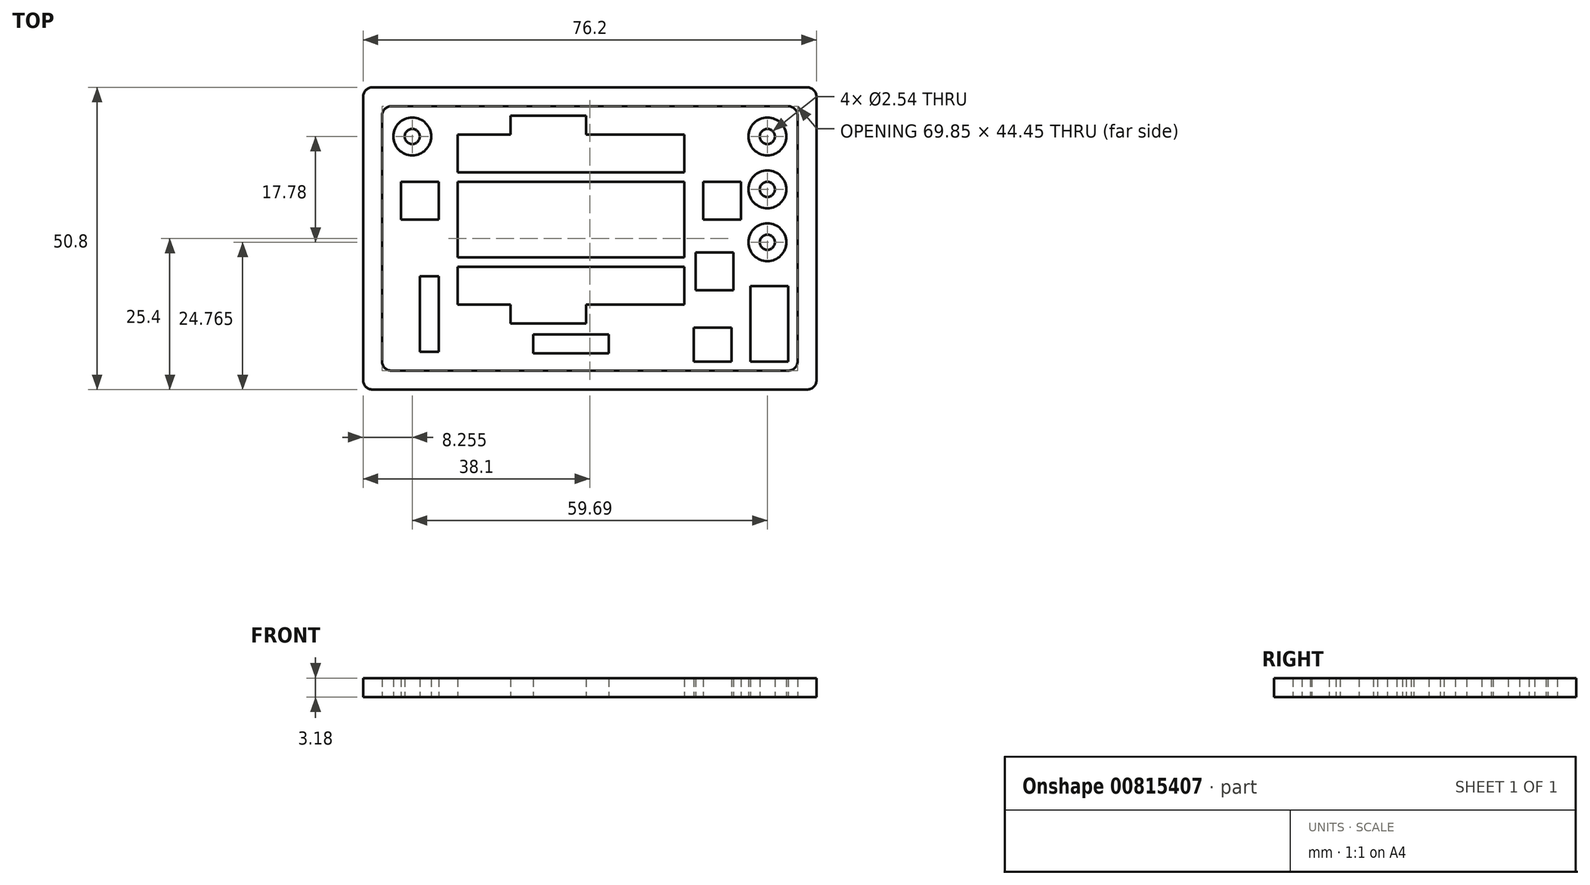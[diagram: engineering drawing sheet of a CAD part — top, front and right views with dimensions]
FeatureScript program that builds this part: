
annotation { "Feature Type Name" : "Feature", "Feature Type Description" : "" }
export const myFeature = defineFeature(function(context is Context, id is Id, definition is map)
    precondition{}
    {
        {
            var Q0;
            Q0=qCreatedBy(makeId("Top.planeOp"),FACE);
            var sketch = newSketch(context, id + "F0", { "sketchPlane" : qUnion([Q0])});
            skLineSegment(sketch, "E0.bottom", {"start": v(1.59, 0) * mm, "end": v(74.61, 0) * mm});
            skLineSegment(sketch, "E0.top", {"start": v(1.59, 50.8) * mm, "end": v(74.61, 50.8) * mm});
            skLineSegment(sketch, "E0.left", {"start": v(0, 1.59) * mm, "end": v(0, 49.21) * mm});
            skLineSegment(sketch, "E0.right", {"start": v(76.2, 1.59) * mm, "end": v(76.2, 49.21) * mm});
            skLineSegment(sketch, "E1.0", {"start": v(73.02, 4.76) * mm, "end": v(73.02, 46.04) * mm});
            skLineSegment(sketch, "E1.1", {"start": v(4.76, 3.17) * mm, "end": v(71.44, 3.17) * mm});
            skLineSegment(sketch, "E1.2", {"start": v(3.17, 4.76) * mm, "end": v(3.17, 46.04) * mm});
            skLineSegment(sketch, "E1.3", {"start": v(4.76, 47.63) * mm, "end": v(71.44, 47.63) * mm});
            skPoint(sketch, "E2.visualSharp", {"position": v(0, 50.8) * mm});
            skArc(sketch, "E2.filletArc", {"start": v(1.59, 50.8) * mm, "mid": v(0.46, 50.34) * mm, "end": v(0, 49.21) * mm});
            skPoint(sketch, "E3.visualSharp", {"position": v(76.2, 50.8) * mm});
            skArc(sketch, "E3.filletArc", {"start": v(76.2, 49.21) * mm, "mid": v(75.74, 50.34) * mm, "end": v(74.61, 50.8) * mm});
            skPoint(sketch, "E4.visualSharp", {"position": v(76.2, 0) * mm});
            skArc(sketch, "E4.filletArc", {"start": v(74.61, 0) * mm, "mid": v(75.74, 0.46) * mm, "end": v(76.2, 1.59) * mm});
            skPoint(sketch, "E5.visualSharp", {"position": v(0, 0) * mm});
            skArc(sketch, "E5.filletArc", {"start": v(0, 1.59) * mm, "mid": v(0.46, 0.46) * mm, "end": v(1.59, 0) * mm});
            skPoint(sketch, "E6.visualSharp", {"position": v(3.17, 3.17) * mm});
            skArc(sketch, "E6.filletArc", {"start": v(3.17, 4.76) * mm, "mid": v(3.64, 3.64) * mm, "end": v(4.76, 3.17) * mm});
            skPoint(sketch, "E7.visualSharp", {"position": v(3.17, 47.63) * mm});
            skArc(sketch, "E7.filletArc", {"start": v(4.76, 47.63) * mm, "mid": v(3.64, 47.16) * mm, "end": v(3.17, 46.04) * mm});
            skPoint(sketch, "E8.visualSharp", {"position": v(73.02, 47.63) * mm});
            skArc(sketch, "E8.filletArc", {"start": v(73.02, 46.04) * mm, "mid": v(72.56, 47.16) * mm, "end": v(71.44, 47.63) * mm});
            skPoint(sketch, "E9.visualSharp", {"position": v(73.02, 3.17) * mm});
            skArc(sketch, "E9.filletArc", {"start": v(71.44, 3.17) * mm, "mid": v(72.56, 3.64) * mm, "end": v(73.02, 4.76) * mm});
            skSolve(sketch);
        }
        {
            var Q0;
            Q0=qSketchRegion(id+"F0",true);
            extrude(context, id + "F1", {"entities" : qUnion([Q0]), "depth" : 3.17 * mm, "offsetDistance" : 25.4 * mm});
        }
        {
            var Q0;
            Q0=qCreatedBy(makeId("Top.planeOp"),FACE);
            var sketch = newSketch(context, id + "F2", { "sketchPlane" : qUnion([Q0])});
            skCircle(sketch, "E10", {"center": v(67.94, 24.77) * mm, "radius": 1.27 * mm});
            skCircle(sketch, "E11", {"center": v(67.94, 24.77) * mm, "radius": 3.18 * mm});
            skCircle(sketch, "E12", {"center": v(8.25, 42.55) * mm, "radius": 1.27 * mm});
            skCircle(sketch, "E13", {"center": v(8.25, 42.55) * mm, "radius": 3.18 * mm});
            skCircle(sketch, "E14", {"center": v(67.94, 42.55) * mm, "radius": 1.27 * mm});
            skCircle(sketch, "E15", {"center": v(67.94, 42.55) * mm, "radius": 3.18 * mm});
            skCircle(sketch, "E16", {"center": v(67.94, 33.66) * mm, "radius": 1.27 * mm});
            skCircle(sketch, "E17", {"center": v(67.94, 33.66) * mm, "radius": 3.18 * mm});
            skSolve(sketch);
        }
        {
            var Q0;
            Q0 = qSketchRegion(id + "F2", true);
            extrude(context, id + "F3", {"entities" : qUnion([Q0]), "depth" : 3.17 * mm, "offsetDistance" : 25.4 * mm});
        }
        {
            var Q0;
            Q0=qCreatedBy(makeId("Top.planeOp"),FACE);
            var sketch = newSketch(context, id + "F4", { "sketchPlane" : qUnion([Q0])});
            skLineSegment(sketch, "E18.bottom", {"start": v(15.87, 34.93) * mm, "end": v(53.97, 34.93) * mm});
            skLineSegment(sketch, "E18.top", {"start": v(15.87, 22.23) * mm, "end": v(53.97, 22.23) * mm});
            skLineSegment(sketch, "E18.left", {"start": v(15.87, 34.93) * mm, "end": v(15.87, 22.22) * mm});
            skLineSegment(sketch, "E18.right", {"start": v(53.97, 34.93) * mm, "end": v(53.97, 22.23) * mm});
            skLineSegment(sketch, "E19.bottom", {"start": v(6.35, 34.93) * mm, "end": v(12.7, 34.93) * mm});
            skLineSegment(sketch, "E19.top", {"start": v(6.35, 28.57) * mm, "end": v(12.7, 28.57) * mm});
            skLineSegment(sketch, "E19.left", {"start": v(6.35, 34.93) * mm, "end": v(6.35, 28.57) * mm});
            skLineSegment(sketch, "E19.right", {"start": v(12.7, 34.93) * mm, "end": v(12.7, 28.57) * mm});
            skLineSegment(sketch, "E20.bottom", {"start": v(57.15, 34.93) * mm, "end": v(63.5, 34.93) * mm});
            skLineSegment(sketch, "E20.top", {"start": v(57.15, 28.58) * mm, "end": v(63.5, 28.58) * mm});
            skLineSegment(sketch, "E20.left", {"start": v(57.15, 34.93) * mm, "end": v(57.15, 28.58) * mm});
            skLineSegment(sketch, "E20.right", {"start": v(63.5, 34.93) * mm, "end": v(63.5, 28.58) * mm});
            skSolve(sketch);
        }
        {
            var Q0;
            Q0 = qSketchRegion(id + "F4", true);
            extrude(context, id + "F5", {"entities" : qUnion([Q0]), "depth" : 3.17 * mm, "offsetDistance" : 25.4 * mm});
        }
        {
            var Q0;
            Q0=qCreatedBy(makeId("Top.planeOp"),FACE);
            var sketch = newSketch(context, id + "F6", { "sketchPlane" : qUnion([Q0])});
            skLineSegment(sketch, "E21.bottom", {"start": v(15.87, 20.64) * mm, "end": v(53.97, 20.64) * mm});
            skLineSegment(sketch, "E21.top", {"start": v(15.87, 14.29) * mm, "end": v(53.97, 14.29) * mm});
            skLineSegment(sketch, "E21.left", {"start": v(15.87, 20.64) * mm, "end": v(15.87, 14.29) * mm});
            skLineSegment(sketch, "E21.right", {"start": v(53.97, 20.64) * mm, "end": v(53.97, 14.29) * mm});
            skLineSegment(sketch, "E22.bottom", {"start": v(15.87, 36.51) * mm, "end": v(53.97, 36.51) * mm});
            skLineSegment(sketch, "E22.top", {"start": v(15.87, 42.86) * mm, "end": v(53.97, 42.86) * mm});
            skLineSegment(sketch, "E22.left", {"start": v(15.87, 36.51) * mm, "end": v(15.87, 42.86) * mm});
            skLineSegment(sketch, "E22.right", {"start": v(53.97, 36.51) * mm, "end": v(53.97, 42.86) * mm});
            skLineSegment(sketch, "E23.bottom", {"start": v(24.76, 14.29) * mm, "end": v(37.46, 14.29) * mm});
            skLineSegment(sketch, "E23.top", {"start": v(24.76, 11.11) * mm, "end": v(37.46, 11.11) * mm});
            skLineSegment(sketch, "E23.left", {"start": v(24.76, 14.29) * mm, "end": v(24.76, 11.11) * mm});
            skLineSegment(sketch, "E23.right", {"start": v(37.46, 14.29) * mm, "end": v(37.46, 11.11) * mm});
            skLineSegment(sketch, "E24.bottom", {"start": v(24.76, 42.86) * mm, "end": v(37.46, 42.86) * mm});
            skLineSegment(sketch, "E24.top", {"start": v(24.76, 46.04) * mm, "end": v(37.46, 46.04) * mm});
            skLineSegment(sketch, "E24.left", {"start": v(24.76, 42.86) * mm, "end": v(24.76, 46.04) * mm});
            skLineSegment(sketch, "E24.right", {"start": v(37.46, 42.86) * mm, "end": v(37.46, 46.04) * mm});
            skLineSegment(sketch, "E25.bottom", {"start": v(65.09, 17.4) * mm, "end": v(71.44, 17.4) * mm});
            skLineSegment(sketch, "E25.top", {"start": v(65.09, 4.7) * mm, "end": v(71.44, 4.7) * mm});
            skLineSegment(sketch, "E25.left", {"start": v(65.09, 17.4) * mm, "end": v(65.09, 4.7) * mm});
            skLineSegment(sketch, "E25.right", {"start": v(71.44, 17.4) * mm, "end": v(71.44, 4.7) * mm});
            skLineSegment(sketch, "E26.bottom", {"start": v(55.56, 10.41) * mm, "end": v(61.91, 10.41) * mm});
            skLineSegment(sketch, "E26.top", {"start": v(55.56, 4.7) * mm, "end": v(61.91, 4.7) * mm});
            skLineSegment(sketch, "E26.left", {"start": v(55.56, 10.41) * mm, "end": v(55.56, 4.7) * mm});
            skLineSegment(sketch, "E26.right", {"start": v(61.91, 10.41) * mm, "end": v(61.91, 4.7) * mm});
            skLineSegment(sketch, "E27.bottom", {"start": v(55.91, 23.03) * mm, "end": v(62.26, 23.03) * mm});
            skLineSegment(sketch, "E27.top", {"start": v(55.91, 16.68) * mm, "end": v(62.26, 16.68) * mm});
            skLineSegment(sketch, "E27.left", {"start": v(55.91, 23.03) * mm, "end": v(55.91, 16.68) * mm});
            skLineSegment(sketch, "E27.right", {"start": v(62.26, 23.03) * mm, "end": v(62.26, 16.68) * mm});
            skSolve(sketch);
        }
        {
            var Q0;
            Q0 = qSketchRegion(id + "F6", true);
            extrude(context, id + "F7", {"entities" : qUnion([Q0]), "depth" : 3.17 * mm, "offsetDistance" : 25.4 * mm});
        }
        {
            var Q0;
            Q0=qCreatedBy(makeId("Top.planeOp"),FACE);
            var sketch = newSketch(context, id + "F8", { "sketchPlane" : qUnion([Q0])});
            skLineSegment(sketch, "E28.bottom", {"start": v(9.52, 19.05) * mm, "end": v(12.7, 19.05) * mm});
            skLineSegment(sketch, "E28.top", {"start": v(9.52, 6.35) * mm, "end": v(12.7, 6.35) * mm});
            skLineSegment(sketch, "E28.left", {"start": v(9.52, 19.05) * mm, "end": v(9.52, 6.35) * mm});
            skLineSegment(sketch, "E28.right", {"start": v(12.7, 19.05) * mm, "end": v(12.7, 6.35) * mm});
            skLineSegment(sketch, "E29.bottom", {"start": v(28.57, 9.25) * mm, "end": v(41.27, 9.25) * mm});
            skLineSegment(sketch, "E29.top", {"start": v(28.57, 6.08) * mm, "end": v(41.27, 6.08) * mm});
            skLineSegment(sketch, "E29.left", {"start": v(28.57, 9.25) * mm, "end": v(28.57, 6.08) * mm});
            skLineSegment(sketch, "E29.right", {"start": v(41.27, 9.25) * mm, "end": v(41.27, 6.08) * mm});
            skSolve(sketch);
        }
        {
            var Q0;
            Q0 = qSketchRegion(id + "F8", true);
            extrude(context, id + "F9", {"entities" : qUnion([Q0]), "depth" : 3.17 * mm, "offsetDistance" : 25.4 * mm});
        }
    });
